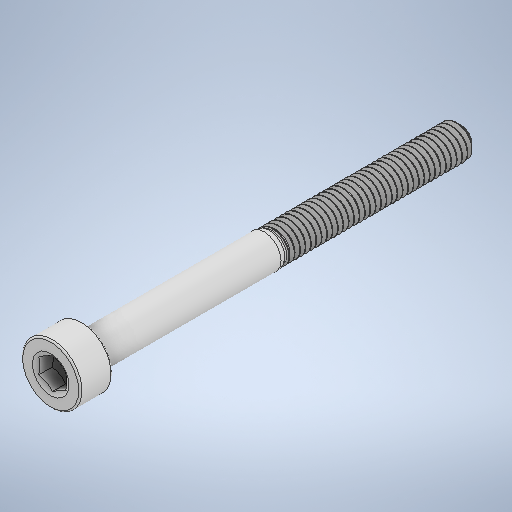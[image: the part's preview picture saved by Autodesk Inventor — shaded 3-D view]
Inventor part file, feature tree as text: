
AUTODESK INVENTOR PART (.ipt)
format: ipt  version: 2025 (Build 290162000, 162)  size: 591,360 bytes
history: native  units: in
note: dims shown in document units (in); Inventor stores cm internally (conversion verified against a paired STEP export)
features: fillet x1
ambient origin geometry x8: Origin, YZ Plane, XZ Plane, XY Plane, X Axis, Y Axis, Z Axis, Center Point
bodies: Solid1 (feature_tree)
feature tree (1):
  fillet  "Fillet1"  [1 undecoded]
note: 1 required parameter value undecoded (feature->parameter linkage not recoverable at this tier; creation-order binding heuristic only, values carry confidence <= 0.55)
